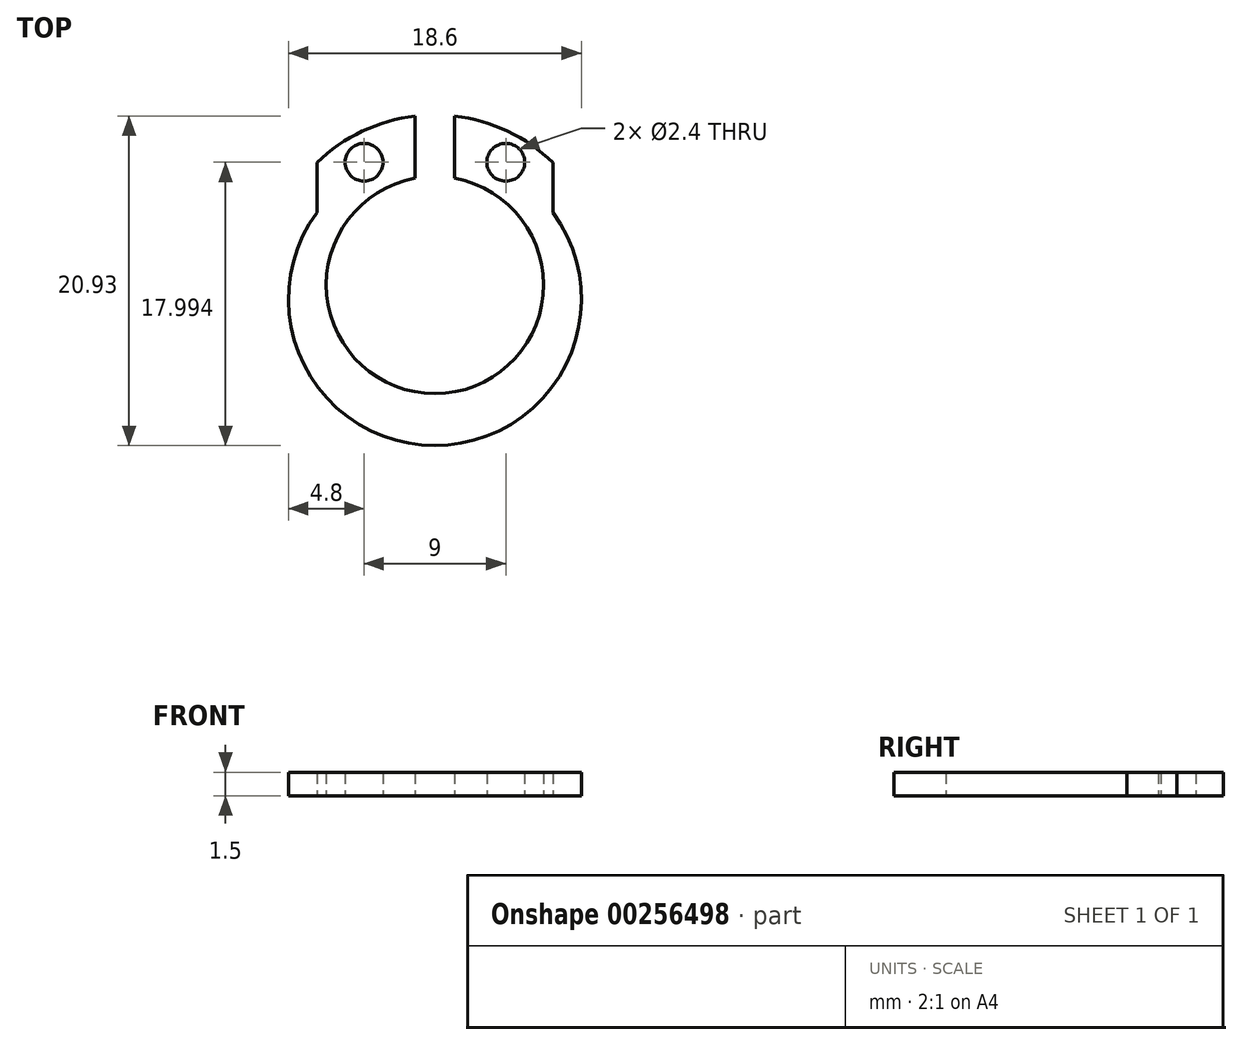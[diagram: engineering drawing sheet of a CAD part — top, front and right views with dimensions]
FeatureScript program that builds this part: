
annotation { "Feature Type Name" : "Feature", "Feature Type Description" : "" }
export const myFeature = defineFeature(function(context is Context, id is Id, definition is map)
    precondition{}
    {
        {
            var Q0;
            Q0=qCreatedBy(makeId("Top.planeOp"),FACE);
            var sketch = newSketch(context, id + "F0", { "sketchPlane" : qUnion([Q0])});
            skCircle(sketch, "E0", {"center": v(0, 0) * mm, "radius": 3 * mm, "construction": true});
            skArc(sketch, "E1", {"start": v(2.5, 2.6) * mm, "mid": v(1.54, 3.25) * mm, "end": v(0.42, 3.58) * mm});
            skArc(sketch, "E2", {"start": v(-0.42, 2.26) * mm, "mid": v(0, -2.3) * mm, "end": v(0.42, 2.26) * mm});
            skCircle(sketch, "E3", {"center": v(-1.5, 2.6) * mm, "radius": 0.4 * mm});
            skCircle(sketch, "E4", {"center": v(1.5, 2.6) * mm, "radius": 0.4 * mm});
            skLineSegment(sketch, "E5", {"start": v(-0.42, 3.58) * mm, "end": v(-0.42, 2.26) * mm});
            skLineSegment(sketch, "E6", {"start": v(0.42, 3.58) * mm, "end": v(0.42, 2.26) * mm});
            skLineSegment(sketch, "E7", {"start": v(-2.5, 2.6) * mm, "end": v(-2.5, 1.53) * mm});
            skLineSegment(sketch, "E8", {"start": v(2.5, 2.6) * mm, "end": v(2.5, 1.53) * mm});
            skArc(sketch, "E9.trimOffspring", {"start": v(-0.42, 3.58) * mm, "mid": v(-1.54, 3.25) * mm, "end": v(-2.5, 2.6) * mm});
            skArc(sketch, "E10.trimOffspring", {"start": v(-2.5, 1.53) * mm, "mid": v(0, -3.4) * mm, "end": v(2.5, 1.53) * mm});
            skSolve(sketch);
        }
        {
            var Q0;
            Q0=makeQuery(id+"F0.imprint","IMPRINT",FACE,{"disambiguationData":[TD([[makeQuery(id+"F0.imprint","IMPRINT",EDGE,{"derivedFrom":sQuery(id+"F0.wireOp",EDGE,"E1")}),1.0]])]});
            extrude(context, id + "F1", {"entities" : qUnion([Q0]), "depth" : 0.5 * mm});
        }
        {
            var Q0;
            Q0=makeQuery(id+"F1.opExtrude","SWEPT_BODY",BODY,{"disambiguationData":[OSD([sQuery(id+"F0.wireOp",EDGE,"E1"),sQuery(id+"F0.wireOp",EDGE,"E2"),sQuery(id+"F0.wireOp",EDGE,"E3"),sQuery(id+"F0.wireOp",EDGE,"E4"),sQuery(id+"F0.wireOp",EDGE,"E5"),sQuery(id+"F0.wireOp",EDGE,"E6"),sQuery(id+"F0.wireOp",EDGE,"E7"),sQuery(id+"F0.wireOp",EDGE,"E8"),sQuery(id+"F0.wireOp",EDGE,"E9.trimOffspring"),sQuery(id+"F0.wireOp",EDGE,"E10.trimOffspring")])]});
            var Q1;
            Q1=qCreatedBy(makeId("Origin.pointOp"),VERTEX);
            transform(context, id + "F2", {"entities" : qUnion([Q0]), "transformType" : TransformType.SCALE_UNIFORMLY, "scale" : 3, "makeCopy" : false, "scalePoint" : qUnion([Q1])});
        }
    });
